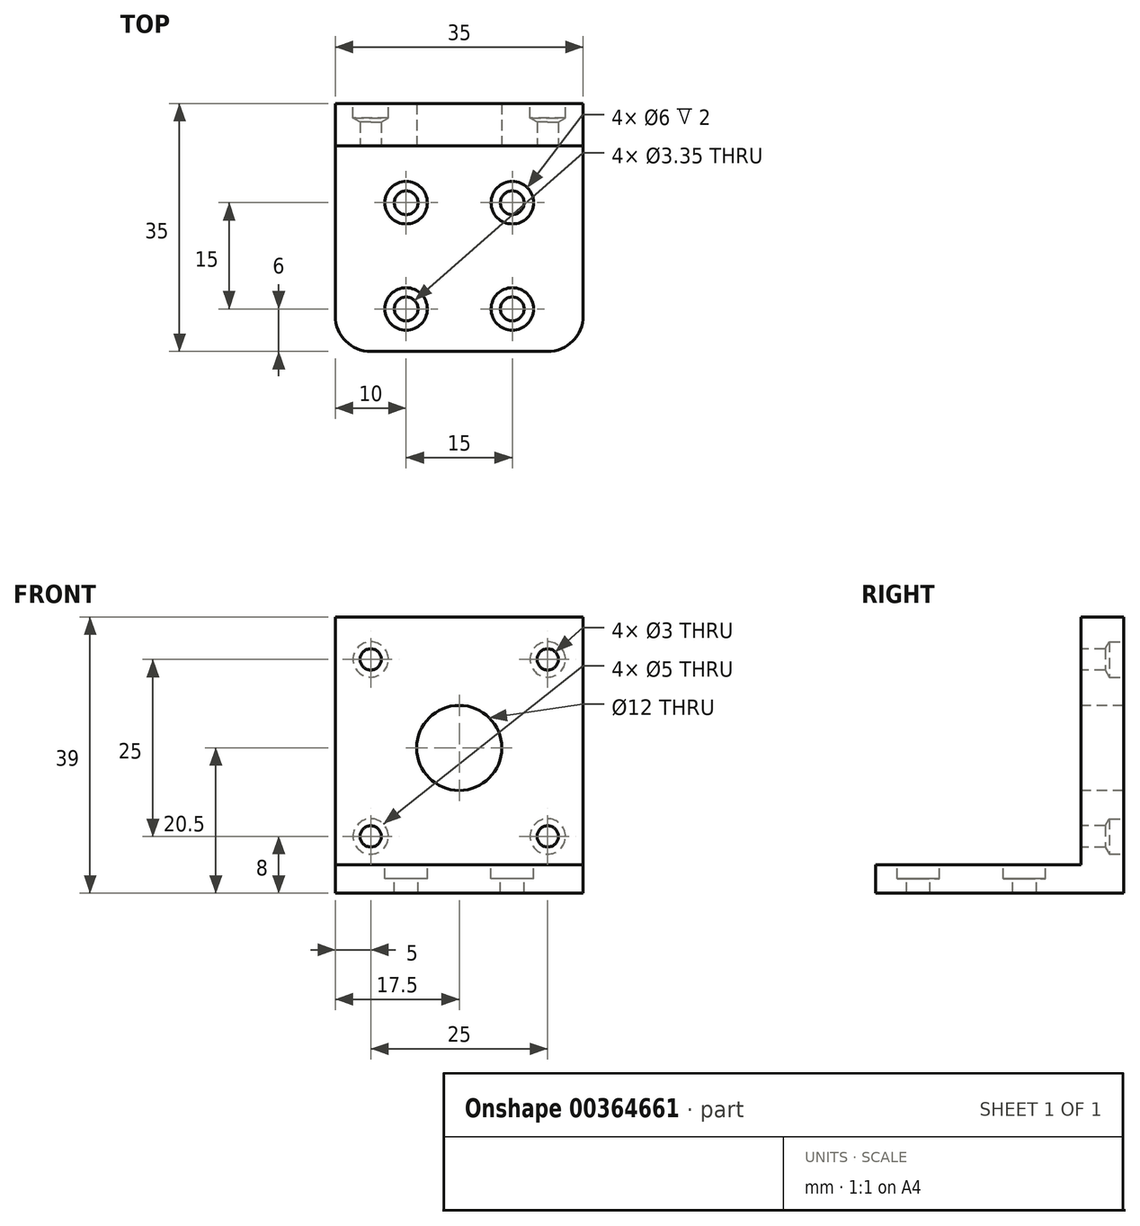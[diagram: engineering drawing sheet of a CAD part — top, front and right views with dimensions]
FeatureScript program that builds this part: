
annotation { "Feature Type Name" : "Feature", "Feature Type Description" : "" }
export const myFeature = defineFeature(function(context is Context, id is Id, definition is map)
    precondition{}
    {
        {
            var Q0;
            Q0=qCreatedBy(makeId("Top.planeOp"),FACE);
            var sketch = newSketch(context, id + "F0", { "sketchPlane" : qUnion([Q0])});
            skLineSegment(sketch, "E0.bottom", {"start": v(0, 0) * mm, "end": v(35, 0) * mm});
            skLineSegment(sketch, "E0.top", {"start": v(0, 35) * mm, "end": v(35, 35) * mm});
            skLineSegment(sketch, "E0.left", {"start": v(0, 0) * mm, "end": v(0, 35) * mm});
            skLineSegment(sketch, "E0.right", {"start": v(35, 0) * mm, "end": v(35, 35) * mm});
            skSolve(sketch);
        }
        {
            var Q0;
            Q0=qSketchRegion(id+"F0",true);
            extrude(context, id + "F1", {"entities" : qUnion([Q0]), "depth" : 4 * mm});
        }
        {
            var Q0;
            Q0=makeQuery(id+"F1.opExtrude","CAP_FACE",FACE,{"disambiguationData":[OSD([sQuery(id+"F0.wireOp",EDGE,"E0.bottom"),sQuery(id+"F0.wireOp",EDGE,"E0.top"),sQuery(id+"F0.wireOp",EDGE,"E0.left"),sQuery(id+"F0.wireOp",EDGE,"E0.right")])],"isStart":false});
            var sketch = newSketch(context, id + "F2", { "sketchPlane" : qUnion([Q0])});
            skCircle(sketch, "E1", {"center": v(10, 21) * mm, "radius": 1.68 * mm});
            skCircle(sketch, "E2", {"center": v(25, 21) * mm, "radius": 1.68 * mm});
            skCircle(sketch, "E3", {"center": v(10, 6) * mm, "radius": 1.68 * mm});
            skCircle(sketch, "E4", {"center": v(25, 6) * mm, "radius": 1.68 * mm});
            skLineSegment(sketch, "E5", {"start": v(10, 21) * mm, "end": v(0, 21) * mm});
            skLineSegment(sketch, "E6", {"start": v(25, 6) * mm, "end": v(35, 6) * mm});
            skCircle(sketch, "E7", {"center": v(10, 21) * mm, "radius": 3 * mm});
            skCircle(sketch, "E8", {"center": v(25, 21) * mm, "radius": 3 * mm});
            skCircle(sketch, "E9", {"center": v(10, 6) * mm, "radius": 3 * mm});
            skCircle(sketch, "E10", {"center": v(25, 6) * mm, "radius": 3 * mm});
            skLineSegment(sketch, "E11", {"start": v(10, 6) * mm, "end": v(10, 0) * mm});
            skSolve(sketch);
        }
        {
            var Q0;
            Q0=makeQuery(id+"F1.opExtrude","CAP_FACE",FACE,{"disambiguationData":[OSD([sQuery(id+"F0.wireOp",EDGE,"E0.bottom"),sQuery(id+"F0.wireOp",EDGE,"E0.top"),sQuery(id+"F0.wireOp",EDGE,"E0.left"),sQuery(id+"F0.wireOp",EDGE,"E0.right")])],"isStart":false});
            var sketch = newSketch(context, id + "F3", { "sketchPlane" : qUnion([Q0])});
            skLineSegment(sketch, "E12.bottom", {"start": v(0, 35) * mm, "end": v(35, 35) * mm});
            skLineSegment(sketch, "E12.top", {"start": v(0, 29) * mm, "end": v(35, 29) * mm});
            skLineSegment(sketch, "E12.left", {"start": v(0, 35) * mm, "end": v(0, 29) * mm});
            skLineSegment(sketch, "E12.right", {"start": v(35, 35) * mm, "end": v(35, 29) * mm});
            skSolve(sketch);
        }
        {
            var Q0;
            Q0=makeQuery(id+"F2.imprint","IMPRINT",FACE,{"disambiguationData":[TD([[makeQuery(id+"F2.imprint","IMPRINT",EDGE,{"derivedFrom":sQuery(id+"F2.wireOp",EDGE,"E1")}),-1.0]])]});
            var Q1;
            Q1=makeQuery(id+"F2.imprint","IMPRINT",FACE,{"disambiguationData":[TD([[makeQuery(id+"F2.imprint","IMPRINT",EDGE,{"derivedFrom":sQuery(id+"F2.wireOp",EDGE,"E2")}),-1.0]])]});
            var Q2;
            Q2=makeQuery(id+"F2.imprint","IMPRINT",FACE,{"disambiguationData":[TD([[makeQuery(id+"F2.imprint","IMPRINT",EDGE,{"derivedFrom":sQuery(id+"F2.wireOp",EDGE,"E4")}),-1.0]])]});
            var Q3;
            Q3=makeQuery(id+"F2.imprint","IMPRINT",FACE,{"disambiguationData":[TD([[makeQuery(id+"F2.imprint","IMPRINT",EDGE,{"derivedFrom":sQuery(id+"F2.wireOp",EDGE,"E3")}),-1.0]])]});
            extrude(context, id + "F4", {"entities" : qUnion([Q0, Q1, Q2, Q3]), "operationType" : NewBodyOperationType.REMOVE, "oppositeDirection" : true, "depth" : 2 * mm});
        }
        {
            var Q0;
            Q0=makeQuery(id+"F1.opExtrude","SWEPT_EDGE",EDGE,{"disambiguationData":[OSD([sQuery(id+"F0.wireOp",EDGE,"E0.bottom"),sQuery(id+"F0.wireOp",EDGE,"E0.left")])]});
            var Q1;
            Q1=makeQuery(id+"F1.opExtrude","SWEPT_EDGE",EDGE,{"disambiguationData":[OSD([sQuery(id+"F0.wireOp",EDGE,"E0.bottom"),sQuery(id+"F0.wireOp",EDGE,"E0.right")])]});
            fillet(context, id + "F5", {"entities" : qUnion([Q0, Q1]), "radius" : 5 * mm, "tangentPropagation" : true, "allowEdgeOverflow" : false});
        }
        {
            var Q0;
            Q0=makeQuery(id+"F2.imprint","IMPRINT",FACE,{"disambiguationData":[TD([[makeQuery(id+"F2.imprint","IMPRINT",EDGE,{"derivedFrom":sQuery(id+"F2.wireOp",EDGE,"E1")}),1.0]])]});
            var Q1;
            Q1=makeQuery(id+"F2.imprint","IMPRINT",FACE,{"disambiguationData":[TD([[makeQuery(id+"F2.imprint","IMPRINT",EDGE,{"derivedFrom":sQuery(id+"F2.wireOp",EDGE,"E2")}),1.0]])]});
            var Q2;
            Q2=makeQuery(id+"F2.imprint","IMPRINT",FACE,{"disambiguationData":[TD([[makeQuery(id+"F2.imprint","IMPRINT",EDGE,{"derivedFrom":sQuery(id+"F2.wireOp",EDGE,"E4")}),1.0]])]});
            var Q3;
            Q3=makeQuery(id+"F2.imprint","IMPRINT",FACE,{"disambiguationData":[TD([[makeQuery(id+"F2.imprint","IMPRINT",EDGE,{"derivedFrom":sQuery(id+"F2.wireOp",EDGE,"E3")}),1.0]])]});
            extrude(context, id + "F6", {"entities" : qUnion([Q0, Q1, Q2, Q3]), "operationType" : NewBodyOperationType.REMOVE, "endBound" : BoundingType.SYMMETRIC, "oppositeDirection" : true, "depth" : 25 * mm});
        }
        {
            var Q0;
            Q0=makeQuery(id+"F3.imprint","IMPRINT",FACE,{"disambiguationData":[TD([[makeQuery(id+"F3.imprint","IMPRINT",EDGE,{"derivedFrom":sQuery(id+"F3.wireOp",EDGE,"E12.bottom")}),-1.0]])]});
            extrude(context, id + "F7", {"entities" : qUnion([Q0]), "operationType" : NewBodyOperationType.ADD, "depth" : 35 * mm});
        }
        {
            var Q0;
            Q0=makeQuery(id+"F7.opExtrude","SWEPT_FACE",FACE,{"disambiguationData":[OSD([sQuery(id+"F3.wireOp",EDGE,"E12.top")])]});
            var sketch = newSketch(context, id + "F8", { "sketchPlane" : qUnion([Q0])});
            skLineSegment(sketch, "E13", {"start": v(17.5, 4) * mm, "end": v(1, 4) * mm, "construction": true});
            skLineSegment(sketch, "E14", {"start": v(1, 4) * mm, "end": v(1, 37) * mm, "construction": true});
            skLineSegment(sketch, "E15", {"start": v(1, 37) * mm, "end": v(34, 37) * mm, "construction": true});
            skLineSegment(sketch, "E16", {"start": v(34, 37) * mm, "end": v(34, 4) * mm, "construction": true});
            skLineSegment(sketch, "E17", {"start": v(1, 37) * mm, "end": v(34, 4) * mm, "construction": true});
            skLineSegment(sketch, "E18", {"start": v(34, 37) * mm, "end": v(1, 4) * mm, "construction": true});
            skCircle(sketch, "E19", {"center": v(17.5, 20.5) * mm, "radius": 6 * mm});
            skLineSegment(sketch, "E20", {"start": v(17.5, 4) * mm, "end": v(17.5, 8) * mm, "construction": true});
            skLineSegment(sketch, "E21", {"start": v(17.5, 8) * mm, "end": v(5, 8) * mm});
            skLineSegment(sketch, "E22", {"start": v(5, 8) * mm, "end": v(30, 8) * mm, "construction": true});
            skLineSegment(sketch, "E23", {"start": v(30, 8) * mm, "end": v(30, 33) * mm, "construction": true});
            skLineSegment(sketch, "E24", {"start": v(30, 33) * mm, "end": v(5, 33) * mm, "construction": true});
            skCircle(sketch, "E25", {"center": v(5, 33) * mm, "radius": 1.5 * mm});
            skCircle(sketch, "E26", {"center": v(30, 33) * mm, "radius": 1.5 * mm});
            skCircle(sketch, "E27", {"center": v(30, 8) * mm, "radius": 1.5 * mm});
            skCircle(sketch, "E28", {"center": v(5, 8) * mm, "radius": 1.5 * mm});
            skSolve(sketch);
        }
        {
            var Q0;
            Q0=makeQuery(id+"F8.imprint","IMPRINT",FACE,{"disambiguationData":[TD([[makeQuery(id+"F8.imprint","IMPRINT",EDGE,{"derivedFrom":sQuery(id+"F8.wireOp",EDGE,"E19")}),1.0]])]});
            var Q1;
            Q1=makeQuery(id+"F8.imprint","IMPRINT",FACE,{"disambiguationData":[TD([[makeQuery(id+"F8.imprint","IMPRINT",EDGE,{"derivedFrom":sQuery(id+"F8.wireOp",EDGE,"E26")}),1.0]])]});
            var Q2;
            Q2=makeQuery(id+"F8.imprint","IMPRINT",FACE,{"disambiguationData":[TD([[makeQuery(id+"F8.imprint","IMPRINT",EDGE,{"derivedFrom":sQuery(id+"F8.wireOp",EDGE,"E25")}),1.0]])]});
            var Q3;
            Q3=makeQuery(id+"F8.imprint","IMPRINT",FACE,{"disambiguationData":[TD([[makeQuery(id+"F8.imprint","IMPRINT",EDGE,{"derivedFrom":sQuery(id+"F8.wireOp",EDGE,"E28")}),1.0]])]});
            var Q4;
            Q4=makeQuery(id+"F8.imprint","IMPRINT",FACE,{"disambiguationData":[TD([[makeQuery(id+"F8.imprint","IMPRINT",EDGE,{"derivedFrom":sQuery(id+"F8.wireOp",EDGE,"E27")}),1.0]])]});
            var Q5;
            Q5=sQuery(id+"F8.wireOp",EDGE,"E19");
            extrude(context, id + "F9", {"entities" : qUnion([Q0, Q1, Q2, Q3, Q4]), "operationType" : NewBodyOperationType.REMOVE, "surfaceEntities" : qUnion([Q5]), "endBound" : BoundingType.THROUGH_ALL, "oppositeDirection" : true, "depth" : 25 * mm});
        }
        {
            var Q0;
            Q0=makeQuery(id+"F7.boolean.opBoolean","MERGE",FACE,{"derivedFrom":[makeQuery(id+"F1.opExtrude","SWEPT_FACE",FACE,{"disambiguationData":[OSD([sQuery(id+"F0.wireOp",EDGE,"E0.top")])]}),makeQuery(id+"F7.opExtrude","SWEPT_FACE",FACE,{"disambiguationData":[OSD([sQuery(id+"F3.wireOp",EDGE,"E12.bottom")])]})]});
            var sketch = newSketch(context, id + "F10", { "sketchPlane" : qUnion([Q0])});
            skLineSegment(sketch, "E29", {"start": v(-30, 33) * mm, "end": v(-5, 33) * mm, "construction": true});
            skLineSegment(sketch, "E30", {"start": v(-5, 33) * mm, "end": v(-5, 8) * mm, "construction": true});
            skLineSegment(sketch, "E31", {"start": v(-5, 8) * mm, "end": v(-30, 8) * mm, "construction": true});
            skLineSegment(sketch, "E32", {"start": v(-30, 8) * mm, "end": v(-30, 33) * mm, "construction": true});
            skSolve(sketch);
        }
        {
            var Q0;
            Q0=sQuery(id+"F10.wireOp",VERTEX,"E32.end");
            var Q1;
            Q1=sQuery(id+"F10.wireOp",VERTEX,"E32.start");
            var Q2;
            Q2=sQuery(id+"F10.wireOp",VERTEX,"E31.start");
            var Q3;
            Q3=sQuery(id+"F10.wireOp",VERTEX,"E30.start");
            var Q4;
            Q4=makeQuery(id+"F1.opExtrude","SWEPT_BODY",BODY,{"disambiguationData":[OSD([sQuery(id+"F0.wireOp",EDGE,"E0.bottom"),sQuery(id+"F0.wireOp",EDGE,"E0.top"),sQuery(id+"F0.wireOp",EDGE,"E0.left"),sQuery(id+"F0.wireOp",EDGE,"E0.right")])]});
            hole(context, id + "F11", {"style" : HoleStyle.SIMPLE, "endStyle" : HoleEndStyle.BLIND, "holeDiameter" : 5 * mm, "holeDepth" : 2 * mm, "isTappedThrough" : true, "tappedDepth" : 12 * mm, "tapClearance" : 3, "locations" : qUnion([Q0, Q1, Q2, Q3]), "scope" : qUnion([Q4])});
        }
    });
